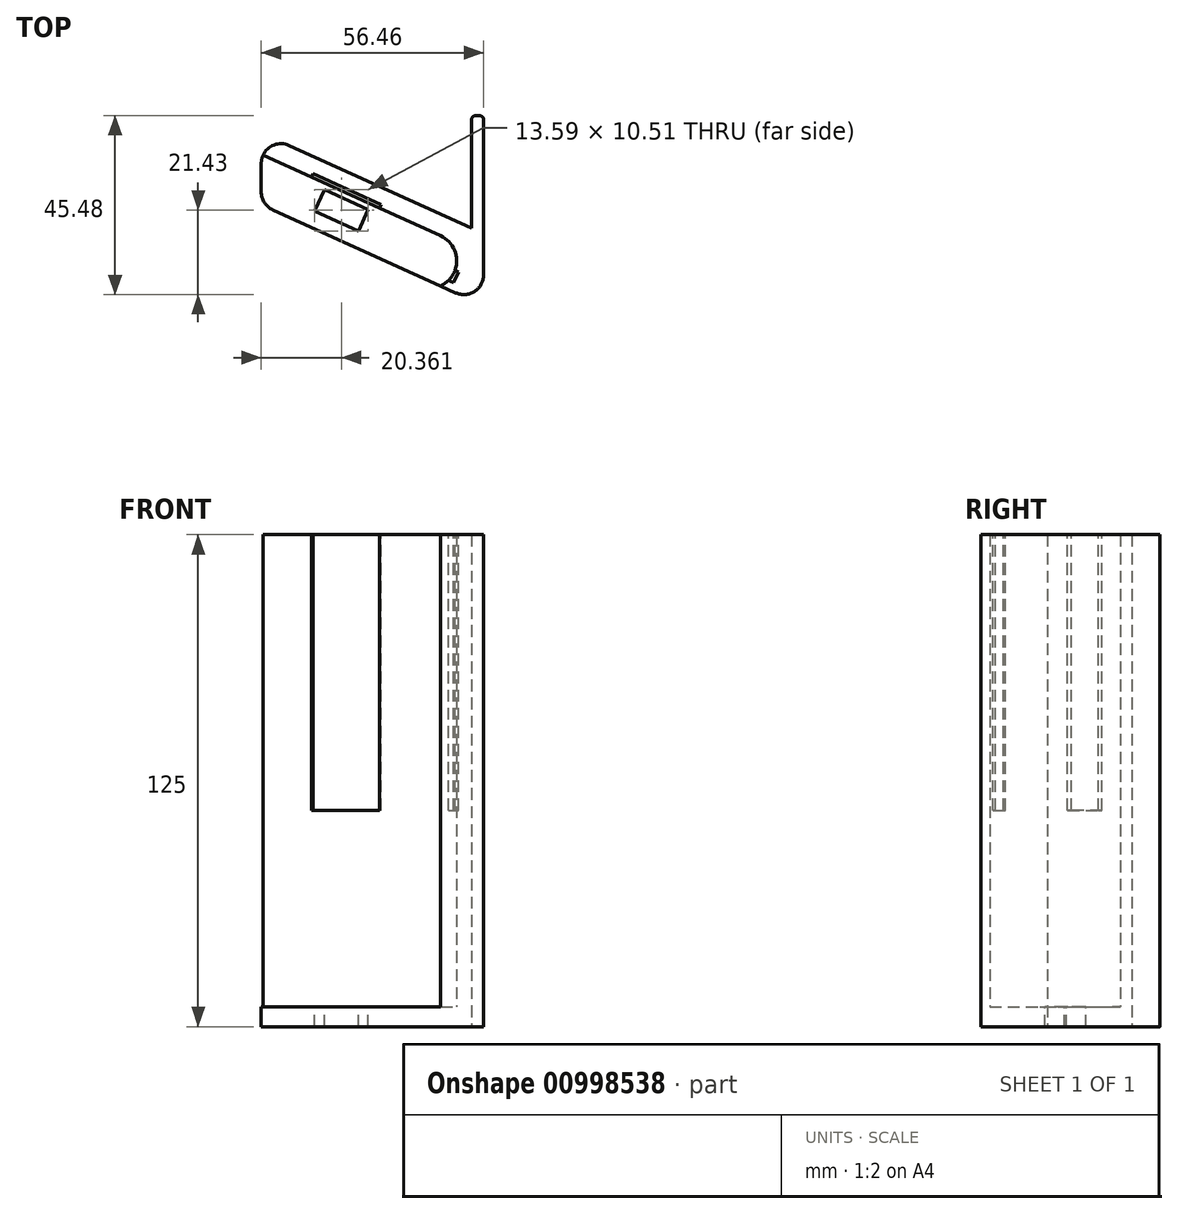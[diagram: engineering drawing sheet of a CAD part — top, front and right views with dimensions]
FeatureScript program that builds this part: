
annotation { "Feature Type Name" : "Feature", "Feature Type Description" : "" }
export const myFeature = defineFeature(function(context is Context, id is Id, definition is map)
    precondition{}
    {
        {
            var Q0;
            Q0=qCreatedBy(makeId("Right.planeOp"),FACE);
            var sketch = newSketch(context, id + "F0", { "sketchPlane" : qUnion([Q0])});
            skLineSegment(sketch, "E0", {"start": v(0, 0) * mm, "end": v(-18.24, 0) * mm});
            skLineSegment(sketch, "E1", {"start": v(-18.24, 0) * mm, "end": v(-13.28, 10.93) * mm});
            skLineSegment(sketch, "E2", {"start": v(-0.53, 10.93) * mm, "end": v(20.13, 56.46) * mm});
            skLineSegment(sketch, "E3", {"start": v(20.13, 56.46) * mm, "end": v(25.62, 56.46) * mm});
            skLineSegment(sketch, "E4", {"start": v(25.62, 56.46) * mm, "end": v(0, 0) * mm});
            skArc(sketch, "E5", {"start": v(-0.53, 10.93) * mm, "mid": v(-6.9, 6.82) * mm, "end": v(-13.28, 10.93) * mm});
            skLineSegment(sketch, "E6", {"start": v(0, 0) * mm, "end": v(30, 0) * mm});
            skLineSegment(sketch, "E7", {"start": v(30, 0) * mm, "end": v(30, 3) * mm});
            skLineSegment(sketch, "E8", {"start": v(30, 3) * mm, "end": v(1.36, 3) * mm});
            skSolve(sketch);
        }
        {
            var Q0;
            Q0=makeQuery(id+"F0.imprint","IMPRINT",FACE,{"disambiguationData":[TD([[makeQuery(id+"F0.imprint","IMPRINT",EDGE,{"derivedFrom":sQuery(id+"F0.wireOp",EDGE,"E0")}),-1.0]])]});
            var Q1;
            {var subQ0=sQuery(id+"F0.wireOp",EDGE,"E6");Q1=makeQuery(id+"F0.imprint","IMPRINT",FACE,{"disambiguationData":[TD([[makeQuery(id+"F0.imprint","IMPRINT",EDGE,{"derivedFrom":subQ0}),1.0]])]});}
            extrude(context, id + "F1", {"entities" : qUnion([Q0, Q1]), "depth" : 120 * mm, "offsetDistance" : 25 * mm});
        }
        {
            var Q0;
            Q0=qCreatedBy(makeId("Right.planeOp"),FACE);
            var sketch = newSketch(context, id + "F2", { "sketchPlane" : qUnion([Q0])});
            skLineSegment(sketch, "E9", {"start": v(25.62, 56.46) * mm, "end": v(7.38, 56.46) * mm});
            skLineSegment(sketch, "E10", {"start": v(7.38, 56.46) * mm, "end": v(-13.28, 10.93) * mm});
            skLineSegment(sketch, "E11", {"start": v(-13.28, 10.93) * mm, "end": v(-18.24, 0) * mm});
            skLineSegment(sketch, "E12", {"start": v(-18.24, 0) * mm, "end": v(0, 0) * mm});
            skLineSegment(sketch, "E13", {"start": v(0, 0) * mm, "end": v(25.62, 56.46) * mm});
            skLineSegment(sketch, "E14", {"start": v(6.16, 29.3) * mm, "end": v(0.7, 31.78) * mm});
            skLineSegment(sketch, "E15", {"start": v(0.7, 31.78) * mm, "end": v(5.74, 42.9) * mm});
            skLineSegment(sketch, "E16", {"start": v(5.74, 42.9) * mm, "end": v(11.2, 40.41) * mm});
            skLineSegment(sketch, "E17", {"start": v(11.2, 40.41) * mm, "end": v(6.16, 29.3) * mm});
            skLineSegment(sketch, "E18", {"start": v(15.2, 62.55) * mm, "end": v(-22.68, -20.93) * mm, "construction": true});
            skLineSegment(sketch, "E19", {"start": v(-9.8, 7.45) * mm, "end": v(-18.35, 11.33) * mm, "construction": true});
            skSolve(sketch);
        }
        {
            var Q0;
            Q0=makeQuery(id+"F0.imprint","IMPRINT",FACE,{"disambiguationData":[TD([[makeQuery(id+"F0.imprint","IMPRINT",EDGE,{"derivedFrom":sQuery(id+"F0.wireOp",EDGE,"E0")}),-1.0]])]});
            var Q1;
            Q1=makeQuery(id+"F2.imprint","IMPRINT",FACE,{"disambiguationData":[TD([[makeQuery(id+"F2.imprint","IMPRINT",EDGE,{"derivedFrom":sQuery(id+"F2.wireOp",EDGE,"E9")}),1.0]])]});
            extrude(context, id + "F3", {"entities" : qUnion([Q0, Q1]), "operationType" : NewBodyOperationType.ADD, "oppositeDirection" : true, "depth" : 5 * mm, "offsetDistance" : 25 * mm});
        }
        {
            var Q0;
            {var subQ0=sQuery(id+"F0.wireOp",EDGE,"E6");Q0=makeQuery(id+"F0.imprint","IMPRINT",FACE,{"disambiguationData":[TD([[makeQuery(id+"F0.imprint","IMPRINT",EDGE,{"derivedFrom":subQ0}),1.0]])]});}
            var Q1;
            Q1=makeQuery(id+"F3.boolean.opBoolean","MERGE",FACE,{"derivedFrom":[makeQuery(id+"F3.opExtrude","CAP_FACE",FACE,{"disambiguationData":[OSD([sQuery(id+"F0.wireOp",EDGE,"E0"),sQuery(id+"F0.wireOp",EDGE,"E1"),sQuery(id+"F0.wireOp",EDGE,"E2"),sQuery(id+"F0.wireOp",EDGE,"E3"),sQuery(id+"F0.wireOp",EDGE,"E4"),sQuery(id+"F0.wireOp",EDGE,"E5")])],"isStart":false}),makeQuery(id+"F3.opExtrude","CAP_FACE",FACE,{"disambiguationData":[OSD([sQuery(id+"F2.wireOp",EDGE,"E9"),sQuery(id+"F2.wireOp",EDGE,"E10"),sQuery(id+"F2.wireOp",EDGE,"E11"),sQuery(id+"F2.wireOp",EDGE,"E12"),sQuery(id+"F2.wireOp",EDGE,"E13"),sQuery(id+"F2.wireOp",EDGE,"E14"),sQuery(id+"F2.wireOp",EDGE,"E15"),sQuery(id+"F2.wireOp",EDGE,"E16"),sQuery(id+"F2.wireOp",EDGE,"E17")])],"isStart":false})]});
            extrude(context, id + "F4", {"entities" : qUnion([Q0]), "operationType" : NewBodyOperationType.ADD, "endBound" : BoundingType.UP_TO_SURFACE, "oppositeDirection" : true, "depth" : 25 * mm, "endBoundEntityFace" : qUnion([Q1]), "offsetDistance" : 25 * mm});
        }
        {
            var Q0;
            Q0=makeQuery(id+"F1.opExtrude","CAP_FACE",FACE,{"disambiguationData":[OSD([sQuery(id+"F0.wireOp",EDGE,"E0"),sQuery(id+"F0.wireOp",EDGE,"E1"),sQuery(id+"F0.wireOp",EDGE,"E2"),sQuery(id+"F0.wireOp",EDGE,"E3"),sQuery(id+"F0.wireOp",EDGE,"E4"),sQuery(id+"F0.wireOp",EDGE,"E5"),sQuery(id+"F0.wireOp",EDGE,"E6"),sQuery(id+"F0.wireOp",EDGE,"E7"),sQuery(id+"F0.wireOp",EDGE,"E8")])],"isStart":false});
            var sketch = newSketch(context, id + "F5", { "sketchPlane" : qUnion([Q0])});
            skLineSegment(sketch, "E20", {"start": v(-11.88, 8.9) * mm, "end": v(-12.48, 7.58) * mm});
            skLineSegment(sketch, "E21", {"start": v(-12.48, 7.58) * mm, "end": v(-9.75, 6.34) * mm});
            skLineSegment(sketch, "E22", {"start": v(-9.75, 6.34) * mm, "end": v(-9.34, 7.26) * mm});
            skLineSegment(sketch, "E23", {"start": v(14.35, 43.73) * mm, "end": v(15.26, 43.31) * mm});
            skLineSegment(sketch, "E24", {"start": v(15.26, 43.31) * mm, "end": v(7.41, 26.01) * mm});
            skLineSegment(sketch, "E25", {"start": v(7.41, 26.01) * mm, "end": v(6.5, 26.42) * mm});
            skSolve(sketch);
        }
        {
            var Q0;
            {var subQ0=sQuery(id+"F5.wireOp",EDGE,"E20");Q0=makeQuery(id+"F5.imprint","IMPRINT",FACE,{"disambiguationData":[TD([[makeQuery(id+"F5.imprint","IMPRINT",EDGE,{"derivedFrom":subQ0}),1.0]])]});}
            var Q1;
            {var subQ0=sQuery(id+"F5.wireOp",EDGE,"E23");Q1=makeQuery(id+"F5.imprint","IMPRINT",FACE,{"disambiguationData":[TD([[makeQuery(id+"F5.imprint","IMPRINT",EDGE,{"derivedFrom":subQ0}),-1.0]])]});}
            extrude(context, id + "F6", {"entities" : qUnion([Q0, Q1]), "operationType" : NewBodyOperationType.REMOVE, "oppositeDirection" : true, "depth" : 70 * mm, "offsetDistance" : 25 * mm});
        }
        {
            var Q0;
            {var subQ0=sQuery(id+"F0.wireOp",EDGE,"E1");var subQ1=sQuery(id+"F0.wireOp",EDGE,"E0");Q0=makeQuery(id+"F3.boolean.opBoolean","MERGE",EDGE,{"derivedFrom":[makeQuery(id+"F1.opExtrude","SWEPT_EDGE",EDGE,{"disambiguationData":[OSD([subQ1,subQ0])]}),makeQuery(id+"F3.opExtrude","SWEPT_EDGE",EDGE,{"disambiguationData":[OSD([subQ1,subQ0])]})]});}
            var Q1;
            Q1=makeQuery(id+"F3.opExtrude","SWEPT_EDGE",EDGE,{"disambiguationData":[OSD([sQuery(id+"F2.wireOp",EDGE,"E9"),sQuery(id+"F2.wireOp",EDGE,"E10")])]});
            var Q2;
            {var subQ0=sQuery(id+"F0.wireOp",EDGE,"E4");var subQ1=sQuery(id+"F0.wireOp",EDGE,"E3");Q2=makeQuery(id+"F3.boolean.opBoolean","MERGE",EDGE,{"derivedFrom":[makeQuery(id+"F1.opExtrude","SWEPT_EDGE",EDGE,{"disambiguationData":[OSD([subQ1,subQ0])]}),makeQuery(id+"F3.opExtrude","SWEPT_EDGE",EDGE,{"disambiguationData":[OSD([subQ1,subQ0])]})]});}
            var Q3;
            {var subQ0=sQuery(id+"F0.wireOp",EDGE,"E8");var subQ1=sQuery(id+"F0.wireOp",EDGE,"E4");Q3=makeQuery(id+"F4.boolean.opBoolean","MERGE",EDGE,{"derivedFrom":[makeQuery(id+"F1.opExtrude","SWEPT_EDGE",EDGE,{"disambiguationData":[OSD([subQ1,subQ0])]}),makeQuery(id+"F4.opExtrude","SWEPT_EDGE",EDGE,{"disambiguationData":[OSD([subQ1,subQ0])]})]});}
            fillet(context, id + "F7", {"entities" : qUnion([Q0, Q1, Q2, Q3]), "radius" : 5 * mm, "tangentPropagation" : true, "allowEdgeOverflow" : false});
        }
        {
            var Q0;
            {var subQ0=sQuery(id+"F0.wireOp",EDGE,"E8");var subQ1=sQuery(id+"F0.wireOp",EDGE,"E7");Q0=makeQuery(id+"F4.boolean.opBoolean","MERGE",EDGE,{"derivedFrom":[makeQuery(id+"F1.opExtrude","SWEPT_EDGE",EDGE,{"disambiguationData":[OSD([subQ1,subQ0])]}),makeQuery(id+"F4.opExtrude","SWEPT_EDGE",EDGE,{"disambiguationData":[OSD([subQ1,subQ0])]})]});}
            var Q1;
            {var subQ0=sQuery(id+"F0.wireOp",EDGE,"E7");var subQ1=sQuery(id+"F0.wireOp",EDGE,"E6");Q1=makeQuery(id+"F4.boolean.opBoolean","MERGE",EDGE,{"derivedFrom":[makeQuery(id+"F1.opExtrude","SWEPT_EDGE",EDGE,{"disambiguationData":[OSD([subQ1,subQ0])]}),makeQuery(id+"F4.opExtrude","SWEPT_EDGE",EDGE,{"disambiguationData":[OSD([subQ1,subQ0])]})]});}
            fillet(context, id + "F8", {"entities" : qUnion([Q0, Q1]), "radius" : 1 * mm, "tangentPropagation" : true, "allowEdgeOverflow" : false});
        }
        {
            var Q0;
            Q0=makeQuery(id+"F1.opExtrude","SWEPT_BODY",BODY,{"disambiguationData":[OSD([sQuery(id+"F0.wireOp",EDGE,"E0"),sQuery(id+"F0.wireOp",EDGE,"E1"),sQuery(id+"F0.wireOp",EDGE,"E2"),sQuery(id+"F0.wireOp",EDGE,"E3"),sQuery(id+"F0.wireOp",EDGE,"E4"),sQuery(id+"F0.wireOp",EDGE,"E5"),sQuery(id+"F0.wireOp",EDGE,"E6"),sQuery(id+"F0.wireOp",EDGE,"E7"),sQuery(id+"F0.wireOp",EDGE,"E8")])]});
            var Q1;
            Q1=makeQuery(id+"F4.boolean.opBoolean","MERGE",EDGE,{"derivedFrom":[makeQuery(id+"F3.opExtrude","CAP_EDGE",EDGE,{"disambiguationData":[OSD([sQuery(id+"F0.wireOp",EDGE,"E0")])],"isStart":false}),makeQuery(id+"F4.opExtrude","CAP_EDGE",EDGE,{"disambiguationData":[OSD([sQuery(id+"F0.wireOp",EDGE,"E6")])],"isStart":false})]});
            transform(context, id + "F9", {"entities" : qUnion([Q0]), "transformType" : TransformType.ROTATION, "transformAxis" : qUnion([Q1]), "angle" : 90 * degree, "makeCopy" : false});
        }
    });
